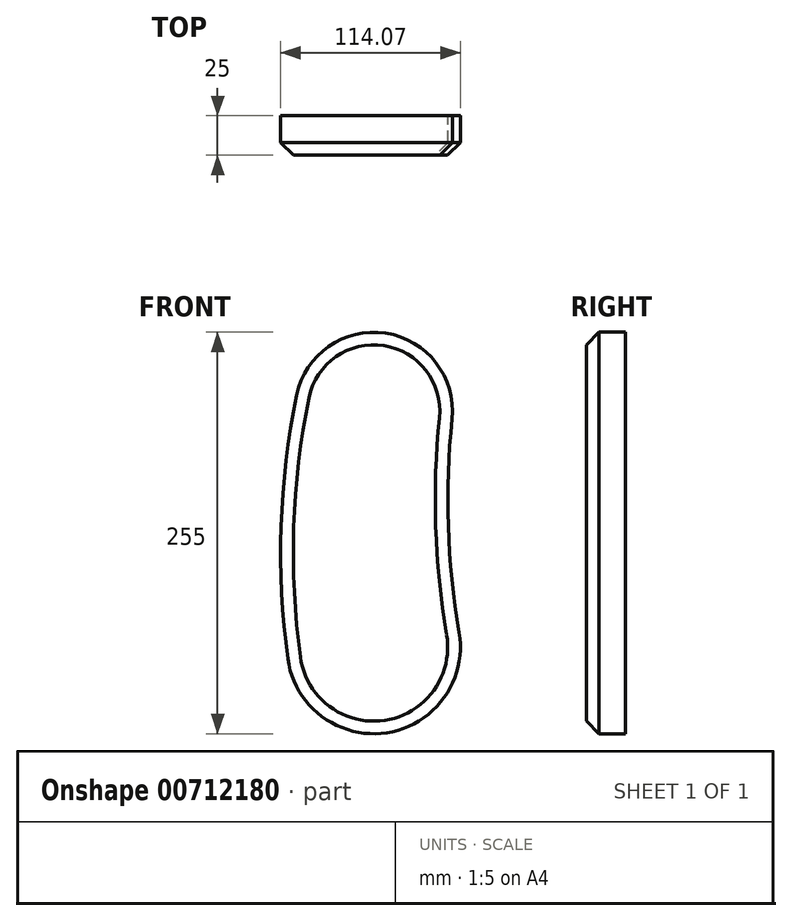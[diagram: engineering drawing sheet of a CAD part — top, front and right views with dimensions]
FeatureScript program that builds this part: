
annotation { "Feature Type Name" : "Feature", "Feature Type Description" : "" }
export const myFeature = defineFeature(function(context is Context, id is Id, definition is map)
    precondition{}
    {
        {
            var Q0;
            Q0=qCreatedBy(makeId("Front.planeOp"),FACE);
            var sketch = newSketch(context, id + "F0", { "sketchPlane" : qUnion([Q0])});
            skArc(sketch, "E0", {"start": v(49.73, -5.14) * mm, "mid": v(7.58, 49.42) * mm, "end": v(-49, 10) * mm});
            skLineSegment(sketch, "E1", {"start": v(0, 0) * mm, "end": v(0, -150) * mm, "construction": true});
            skArc(sketch, "E2", {"start": v(-54.5, -157.43) * mm, "mid": v(8.34, -204.36) * mm, "end": v(54.22, -140.74) * mm});
            skArc(sketch, "E3", {"start": v(-49, 10) * mm, "mid": v(-58.8, -73.49) * mm, "end": v(-54.5, -157.43) * mm});
            skArc(sketch, "E4", {"start": v(49.73, -5.14) * mm, "mid": v(47.35, -73.1) * mm, "end": v(54.22, -140.74) * mm});
            skSolve(sketch);
        }
        {
            var Q0;
            Q0=qSketchRegion(id+"F0",true);
            extrude(context, id + "F1", {"entities" : qUnion([Q0]), "depth" : 25 * mm, "offsetDistance" : 25 * mm});
        }
        {
            var Q0;
            Q0=makeQuery(id+"F1.opExtrude","CAP_EDGE",EDGE,{"disambiguationData":[OSD([sQuery(id+"F0.wireOp",EDGE,"E0")])],"isStart":false});
            chamfer(context, id + "F2", {"entities" : qUnion([Q0]), "width" : 8 * mm, "tangentPropagation" : true});
        }
    });
